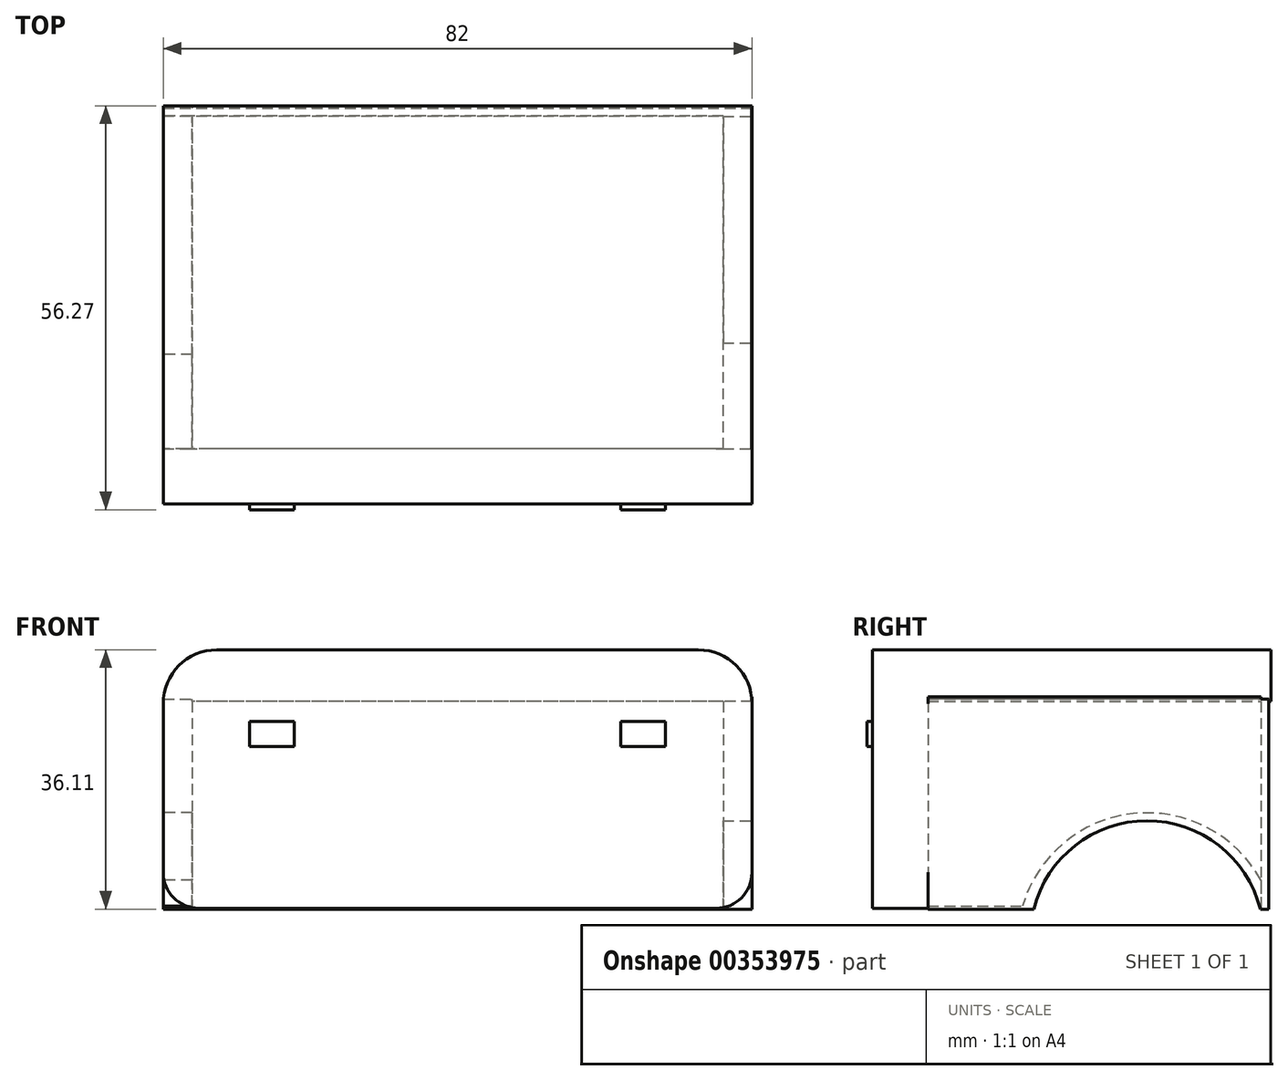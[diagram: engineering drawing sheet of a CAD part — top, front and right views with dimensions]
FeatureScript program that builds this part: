
annotation { "Feature Type Name" : "Feature", "Feature Type Description" : "" }
export const myFeature = defineFeature(function(context is Context, id is Id, definition is map)
    precondition{}
    {
        {
            var Q0;
            Q0=qCreatedBy(makeId("Front.planeOp"),FACE);
            var sketch = newSketch(context, id + "F0", { "sketchPlane" : qUnion([Q0])});
            skLineSegment(sketch, "E0.bottom", {"start": v(41, -18) * mm, "end": v(-41, -18) * mm});
            skLineSegment(sketch, "E0.top", {"start": v(41, 18) * mm, "end": v(-41, 18) * mm});
            skLineSegment(sketch, "E0.left", {"start": v(41, -18) * mm, "end": v(41, 18) * mm});
            skLineSegment(sketch, "E0.right", {"start": v(-41, -18) * mm, "end": v(-41, 18) * mm});
            skPoint(sketch, "E0.middle", {"position": v(0, 0) * mm});
            skSolve(sketch);
        }
        {
            var Q0;
            Q0 = qSketchRegion(id + "F0", true);
            extrude(context, id + "F1", {"entities" : qUnion([Q0]), "depth" : 7.7 * mm});
        }
        {
            var Q0;
            Q0=makeQuery(id+"F1.opExtrude","SWEPT_FACE",FACE,{"disambiguationData":[OSD([sQuery(id+"F0.wireOp",EDGE,"E0.top")])]});
            var sketch = newSketch(context, id + "F2", { "sketchPlane" : qUnion([Q0])});
            skLineSegment(sketch, "E1.bottom", {"start": v(41, -7.33) * mm, "end": v(-41, -7.33) * mm});
            skLineSegment(sketch, "E1.top", {"start": v(41, 46.67) * mm, "end": v(-41, 46.67) * mm});
            skLineSegment(sketch, "E1.left", {"start": v(41, -7.33) * mm, "end": v(41, 46.67) * mm});
            skLineSegment(sketch, "E1.right", {"start": v(-41, -7.33) * mm, "end": v(-41, 46.67) * mm});
            skSolve(sketch);
        }
        {
            var Q0;
            Q0 = qSketchRegion(id + "F2", true);
            extrude(context, id + "F3", {"entities" : qUnion([Q0]), "operationType" : NewBodyOperationType.ADD, "oppositeDirection" : true, "depth" : 7.2 * mm});
        }
        {
            var Q0;
            Q0=makeQuery(id+"F3.boolean.opBoolean","MERGE",EDGE,{"derivedFrom":[makeQuery(id+"F1.opExtrude","SWEPT_EDGE",EDGE,{"disambiguationData":[OSD([sQuery(id+"F0.wireOp",EDGE,"E0.top"),sQuery(id+"F0.wireOp",EDGE,"E0.left")])]}),makeQuery(id+"F3.opExtrude","CAP_EDGE",EDGE,{"disambiguationData":[OSD([sQuery(id+"F2.wireOp",EDGE,"E1.left")])],"isStart":true})]});
            var Q1;
            Q1=makeQuery(id+"F3.boolean.opBoolean","MERGE",EDGE,{"derivedFrom":[makeQuery(id+"F1.opExtrude","SWEPT_EDGE",EDGE,{"disambiguationData":[OSD([sQuery(id+"F0.wireOp",EDGE,"E0.top"),sQuery(id+"F0.wireOp",EDGE,"E0.right")])]}),makeQuery(id+"F3.opExtrude","CAP_EDGE",EDGE,{"disambiguationData":[OSD([sQuery(id+"F2.wireOp",EDGE,"E1.right")])],"isStart":true})]});
            fillet(context, id + "F4", {"entities" : qUnion([Q0, Q1]), "radius" : 7.48 * mm, "tangentPropagation" : true, "allowEdgeOverflow" : false});
        }
        {
            var Q0;
            Q0=makeQuery(id+"F1.opExtrude","SWEPT_EDGE",EDGE,{"disambiguationData":[OSD([sQuery(id+"F0.wireOp",EDGE,"E0.bottom"),sQuery(id+"F0.wireOp",EDGE,"E0.right")])]});
            var Q1;
            Q1=makeQuery(id+"F1.opExtrude","SWEPT_EDGE",EDGE,{"disambiguationData":[OSD([sQuery(id+"F0.wireOp",EDGE,"E0.bottom"),sQuery(id+"F0.wireOp",EDGE,"E0.left")])]});
            fillet(context, id + "F5", {"entities" : qUnion([Q0, Q1]), "radius" : 5 * mm, "tangentPropagation" : true, "allowEdgeOverflow" : false});
        }
        {
            var Q0;
            Q0=makeQuery(id+"F1.opExtrude","CAP_FACE",FACE,{"disambiguationData":[OSD([sQuery(id+"F0.wireOp",EDGE,"E0.bottom"),sQuery(id+"F0.wireOp",EDGE,"E0.top"),sQuery(id+"F0.wireOp",EDGE,"E0.left"),sQuery(id+"F0.wireOp",EDGE,"E0.right")])],"isStart":false});
            var sketch = newSketch(context, id + "F6", { "sketchPlane" : qUnion([Q0])});
            skLineSegment(sketch, "E2.bottom", {"start": v(-28.94, 8) * mm, "end": v(-22.73, 8) * mm});
            skLineSegment(sketch, "E2.top", {"start": v(-28.94, 4.5) * mm, "end": v(-22.73, 4.5) * mm});
            skLineSegment(sketch, "E2.left", {"start": v(-28.94, 8) * mm, "end": v(-28.94, 4.5) * mm});
            skLineSegment(sketch, "E2.right", {"start": v(-22.73, 8) * mm, "end": v(-22.73, 4.5) * mm});
            skLineSegment(sketch, "E3.MirrorCS", {"start": v(22.73, 8) * mm, "end": v(22.73, 4.5) * mm});
            skLineSegment(sketch, "E4.MirrorCS", {"start": v(28.94, 4.5) * mm, "end": v(22.73, 4.5) * mm});
            skLineSegment(sketch, "E5.MirrorCS", {"start": v(28.94, 8) * mm, "end": v(28.94, 4.5) * mm});
            skLineSegment(sketch, "E6.MirrorCS", {"start": v(28.94, 8) * mm, "end": v(22.73, 8) * mm});
            skSolve(sketch);
        }
        {
            var Q0;
            Q0=makeQuery(id+"F6.imprint","IMPRINT",FACE,{"disambiguationData":[TD([[makeQuery(id+"F6.imprint","IMPRINT",EDGE,{"derivedFrom":sQuery(id+"F6.wireOp",EDGE,"E2.bottom")}),-1.0]])]});
            var Q1;
            Q1=makeQuery(id+"F6.imprint","IMPRINT",FACE,{"disambiguationData":[TD([[makeQuery(id+"F6.imprint","IMPRINT",EDGE,{"derivedFrom":sQuery(id+"F6.wireOp",EDGE,"E3.MirrorCS")}),1.0]])]});
            extrude(context, id + "F7", {"entities" : qUnion([Q0, Q1]), "operationType" : NewBodyOperationType.ADD, "depth" : 0.8 * mm});
        }
        {
            var Q0;
            Q0=makeQuery(id+"F3.boolean.opBoolean","MERGE",FACE,{"derivedFrom":[makeQuery(id+"F1.opExtrude","SWEPT_FACE",FACE,{"disambiguationData":[OSD([sQuery(id+"F0.wireOp",EDGE,"E0.left")])]}),makeQuery(id+"F3.opExtrude","SWEPT_FACE",FACE,{"disambiguationData":[OSD([sQuery(id+"F2.wireOp",EDGE,"E1.left")])]})]});
            var sketch = newSketch(context, id + "F8", { "sketchPlane" : qUnion([Q0])});
            skLineSegment(sketch, "E7.bottom", {"start": v(0, 11.44) * mm, "end": v(46.36, 11.44) * mm});
            skLineSegment(sketch, "E7.top", {"start": v(0, -18.11) * mm, "end": v(46.36, -18.11) * mm});
            skLineSegment(sketch, "E7.left", {"start": v(0, 11.44) * mm, "end": v(0, -18.11) * mm});
            skLineSegment(sketch, "E7.right", {"start": v(46.36, 11.44) * mm, "end": v(46.36, -18.11) * mm});
            skArc(sketch, "E8", {"start": v(46.29, -18.11) * mm, "mid": v(30.5, -5.8) * mm, "end": v(14.73, -18.11) * mm});
            skSolve(sketch);
        }
        {
            var Q0;
            Q0=makeQuery(id+"F3.boolean.opBoolean","MERGE",FACE,{"derivedFrom":[makeQuery(id+"F1.opExtrude","SWEPT_FACE",FACE,{"disambiguationData":[OSD([sQuery(id+"F0.wireOp",EDGE,"E0.right")])]}),makeQuery(id+"F3.opExtrude","SWEPT_FACE",FACE,{"disambiguationData":[OSD([sQuery(id+"F2.wireOp",EDGE,"E1.right")])]})]});
            var sketch = newSketch(context, id + "F9", { "sketchPlane" : qUnion([Q0])});
            skLineSegment(sketch, "E9.bottom", {"start": v(0, 11.17) * mm, "end": v(-47.38, 11.17) * mm});
            skLineSegment(sketch, "E9.top", {"start": v(0, -17.68) * mm, "end": v(-47.38, -17.68) * mm});
            skLineSegment(sketch, "E9.left", {"start": v(0, 11.17) * mm, "end": v(0, -17.68) * mm});
            skLineSegment(sketch, "E9.right", {"start": v(-47.38, 11.17) * mm, "end": v(-47.38, -17.68) * mm});
            skArc(sketch, "E10", {"start": v(-13.17, -17.68) * mm, "mid": v(-30.51, -4.7) * mm, "end": v(-47.85, -17.68) * mm});
            skSolve(sketch);
        }
        {
            var Q0;
            {var subQ5=sQuery(id+"F8.wireOp",EDGE,"E7.bottom");Q0=makeQuery(id+"F8.imprint","IMPRINT",FACE,{"disambiguationData":[TD([[makeQuery(id+"F8.imprint","IMPRINT",EDGE,{"derivedFrom":subQ5}),-1.0]])]});}
            extrude(context, id + "F10", {"entities" : qUnion([Q0]), "operationType" : NewBodyOperationType.ADD, "oppositeDirection" : true, "depth" : 4 * mm});
        }
        {
            var Q0;
            {var subQ5=sQuery(id+"F9.wireOp",EDGE,"E9.bottom");Q0=makeQuery(id+"F9.imprint","IMPRINT",FACE,{"disambiguationData":[TD([[makeQuery(id+"F9.imprint","IMPRINT",EDGE,{"derivedFrom":subQ5}),1.0]])]});}
            extrude(context, id + "F11", {"entities" : qUnion([Q0]), "operationType" : NewBodyOperationType.ADD, "oppositeDirection" : true, "depth" : 4 * mm});
        }
        {
            var Q0;
            Q0=makeQuery(id+"F10.opExtrude","SWEPT_FACE",FACE,{"disambiguationData":[OSD([sQuery(id+"F8.wireOp",EDGE,"E7.right")])]});
            var sketch = newSketch(context, id + "F12", { "sketchPlane" : qUnion([Q0])});
            skLineSegment(sketch, "E11.bottom", {"start": v(41, 11.17) * mm, "end": v(-41, 11.17) * mm});
            skLineSegment(sketch, "E11.top", {"start": v(41, -18.11) * mm, "end": v(-41, -18.11) * mm});
            skLineSegment(sketch, "E11.left", {"start": v(41, 11.17) * mm, "end": v(41, -18.11) * mm});
            skLineSegment(sketch, "E11.right", {"start": v(-41, 11.17) * mm, "end": v(-41, -18.11) * mm});
            skSolve(sketch);
        }
        {
            var Q0;
            Q0 = qSketchRegion(id + "F12", true);
            var Q1;
            Q1=makeQuery(id+"F3.opExtrude","SWEPT_FACE",FACE,{"disambiguationData":[OSD([sQuery(id+"F2.wireOp",EDGE,"E1.top")])]});
            extrude(context, id + "F13", {"entities" : qUnion([Q0, Q1]), "operationType" : NewBodyOperationType.ADD, "depth" : 1.1 * mm});
        }
    });
